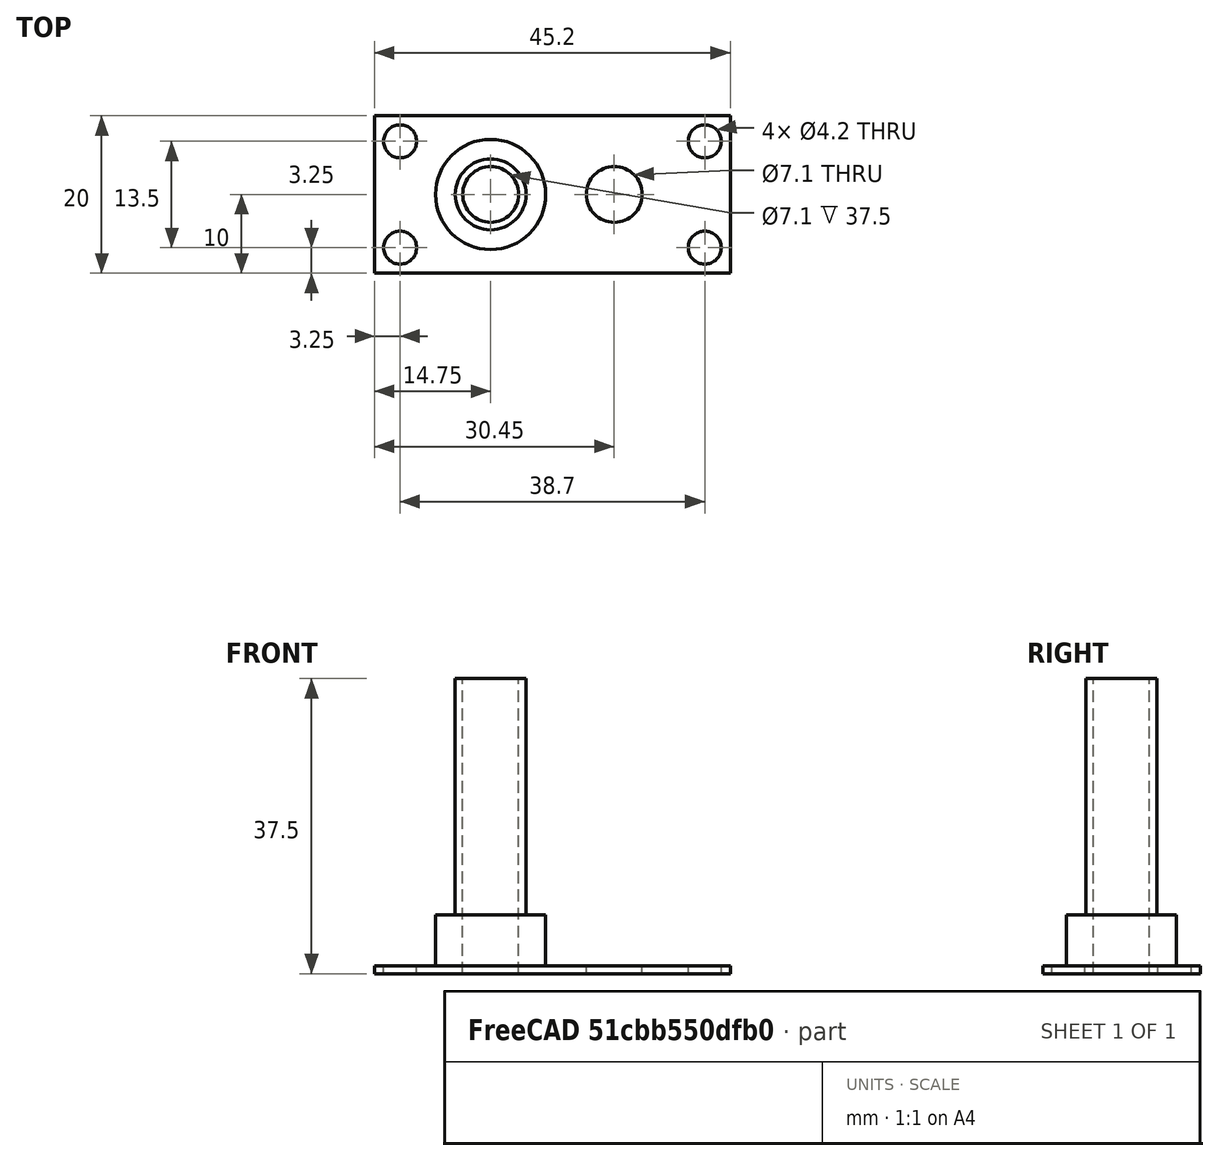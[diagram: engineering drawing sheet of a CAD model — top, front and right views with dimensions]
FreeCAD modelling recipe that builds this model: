
FCSTD DOCUMENT  (FreeCAD 0.17R13522 (Git))
Label: v5_base1_media_con_soportes
License: CreativeCommons Attribution-ShareAlike
LicenseURL: http://creativecommons.org/licenses/by-sa/4.0/
objects: Part::Cut×13, Part::Cylinder×8, Part::Box×6, Part::Feature×6, Part::Fuse×6, Part::Chamfer×3
note: 42 computed .brp shape members not serialized (recipe doc carries the construction recipe); baked Part::Feature solids carry a one-line shape summary decoded from their .brp

FEATURE [Part::Box] Box  label="base"
  AttacherType = Attacher::AttachEngine3D
  Height = 2
  Length = 45.2
  Width = 20
FEATURE [Part::Cylinder] Cylinder  label="cortador izquierda"
  Angle = 360
  AttacherType = Attacher::AttachEngine3D
  Height = 60
  Placement = pos=(14.75,10,-12) rot=(0,0,1;0rad)
  Radius = 3.55
FEATURE [Part::Feature] Cylinder001  label="cortador derecha"
  Placement = pos=(30.45,10,-4) rot=(0,0,1;0rad)
  shape: bbox 7.1 x 7.1 x 10 mm, 3 faces (baked)
FEATURE [Part::Cylinder] Cylinder002  label="sacabocado_abajo_izq"
  Angle = 360
  AttacherType = Attacher::AttachEngine3D
  Height = 10
  Placement = pos=(3,3,-4) rot=(0,0,1;0rad)
  Radius = 1.75
FEATURE [Part::Feature] Cylinder002001  label="sacabocado_abajo_derecha"
  Placement = pos=(42.2,3,-4) rot=(0,0,1;0rad)
  shape: bbox 3.5 x 3.5 x 10 mm, 3 faces (baked)
FEATURE [Part::Feature] Cylinder002002  label="sacabocado_arriba_izq"
  Placement = pos=(3,17,-4) rot=(0,0,1;0rad)
  shape: bbox 3.5 x 3.5 x 10 mm, 3 faces (baked)
FEATURE [Part::Feature] Cylinder002002001  label="sacabocado_arriba_derecha"
  Placement = pos=(42.2,17,-4) rot=(0,0,1;0rad)
  shape: bbox 3.5 x 3.5 x 10 mm, 3 faces (baked)
FEATURE [Part::Cylinder] Cylinder002002002  label="cilindro interior"
  Angle = 360
  AttacherType = Attacher::AttachEngine3D
  Height = 38.5
  Placement = pos=(14.75,10,0) rot=(0,0,1;0rad)
  Radius = 4.5
FEATURE [Part::Cylinder] Cylinder002002003  label="base cilindrica grande"
  Angle = 360
  AttacherType = Attacher::AttachEngine3D
  Height = 8.5
  Placement = pos=(14.75,10,0) rot=(0,0,1;0rad)
  Radius = 7
FEATURE [Part::Cut] Cut
  Base = -> Box
  Refine = true
  Tool = -> Cylinder002
FEATURE [Part::Cut] Cut001
  Base = -> Cut
  Refine = true
  Tool = -> Cylinder002001
FEATURE [Part::Cut] Cut002
  Base = -> Cut001
  Refine = true
  Tool = -> Cylinder001
FEATURE [Part::Cut] Cut003
  Base = -> Cut002
  Refine = true
  Tool = -> Cylinder002002001
FEATURE [Part::Cut] Cut004
  Base = -> Cut003
  Refine = true
  Tool = -> Cylinder002002
FEATURE [Part::Fuse] Fusion
  Base = -> Cylinder002002003
  Refine = true
  Tool = -> Cut004
FEATURE [Part::Fuse] Fusion001
  Base = -> Cylinder002002002
  Refine = true
  Tool = -> Fusion
FEATURE [Part::Cut] Cut005  label="pieza sin soportes"
  Base = -> Fusion001
  Refine = true
  Tool = -> Cylinder
FEATURE [Part::Box] Box001  label="soporte1"
  AttacherType = Attacher::AttachEngine3D
  Height = 10.5
  Length = 5
  Placement = pos=(36.95,7.5,-10.5) rot=(0,0,1;0rad)
  Width = 5
FEATURE [Part::Feature] Box001001  label="soporte2"
  Placement = pos=(18.95,7.5,-10.5) rot=(0,0,1;0rad)
  shape: bbox 5 x 5 x 10.5 mm, 6 faces (baked)
FEATURE [Part::Box] Box001002  label="perforador chavetas"
  AttacherType = Attacher::AttachEngine3D
  Height = 2
  Length = 30
  Placement = pos=(16,8.5,-6.3) rot=(0,0,1;0rad)
  Width = 3
FEATURE [Part::Feature] Box001002001  label="perforador chavetas001"
  Placement = pos=(16,8.5,-6.3) rot=(0,0,1;0rad)
  shape: bbox 30 x 3 x 2 mm, 6 faces (baked)
FEATURE [Part::Cut] Cut006
  Base = -> Box001
  Refine = true
  Tool = -> Box001002
FEATURE [Part::Cut] Cut007
  Base = -> Box001001
  Refine = true
  Tool = -> Box001002001
FEATURE [Part::Fuse] Fusion002
  Base = -> Cut005
  Refine = true
  Tool = -> Cut007
FEATURE [Part::Fuse] Fusion003
  Base = -> Cut006
  Refine = true
  Tool = -> Fusion002
FEATURE [Part::Chamfer] Chamfer
  Base = -> Fusion003
  Edges = 1 edges r=2: [Edge29]
FEATURE [Part::Chamfer] Chamfer001
  Base = -> Chamfer
  Edges = 1 edges r=2: [Edge19]
FEATURE [Part::Chamfer] Chamfer002  label="pieza completa"
  Base = -> Chamfer001
  Edges = 2 edges r=2: [Edge4,Edge10]
FEATURE [Part::Box] Box001002002  label="cortador separa pieza 2"
  AttacherType = Attacher::AttachEngine3D
  Height = 26
  Length = 59
  Placement = pos=(-7.65,-6,-25) rot=(0,0,1;0rad)
  Width = 30
FEATURE [Part::Cut] Cut008
  Base = -> Chamfer002
  Refine = true
  Tool = -> Box001002002
FEATURE [Part::Cylinder] Cylinder002002004  label="Cylinder"
  Angle = 360
  AttacherType = Attacher::AttachEngine3D
  Height = 10
  Placement = pos=(41.95,16.75,-4) rot=(0,0,1;0rad)
  Radius = 2.1
FEATURE [Part::Cylinder] Cylinder002002005  label="Cylinder001"
  Angle = 360
  AttacherType = Attacher::AttachEngine3D
  Height = 10
  Placement = pos=(41.95,3.25,-3) rot=(0,0,1;0rad)
  Radius = 2.1
FEATURE [Part::Cylinder] Cylinder002002006  label="Cylinder002"
  Angle = 360
  AttacherType = Attacher::AttachEngine3D
  Height = 10
  Placement = pos=(3.25,16.75,-3) rot=(0,0,1;0rad)
  Radius = 2.1
FEATURE [Part::Cylinder] Cylinder002002007  label="Cylinder003"
  Angle = 360
  AttacherType = Attacher::AttachEngine3D
  Height = 10
  Placement = pos=(3.25,3.25,-3) rot=(0,0,1;0rad)
  Radius = 2.1
FEATURE [Part::Box] Box001002003  label="Cube"
  AttacherType = Attacher::AttachEngine3D
  Height = 1
  Length = 7
  Placement = pos=(0,0,1) rot=(0,0,1;0rad)
  Width = 20
FEATURE [Part::Fuse] Fusion004
  Base = -> Cut008
  Refine = true
  Tool = -> Box001002003
FEATURE [Part::Box] Box001002004  label="Cube001"
  AttacherType = Attacher::AttachEngine3D
  Height = 1
  Length = 10
  Placement = pos=(35,0,1) rot=(0,0,1;0rad)
  Width = 20
FEATURE [Part::Fuse] Fusion005
  Base = -> Fusion004
  Refine = true
  Tool = -> Box001002004
FEATURE [Part::Cut] Cut009
  Base = -> Fusion005
  Refine = true
  Tool = -> Cylinder002002007
FEATURE [Part::Cut] Cut010
  Base = -> Cut009
  Refine = true
  Tool = -> Cylinder002002006
FEATURE [Part::Cut] Cut011
  Base = -> Cut010
  Refine = true
  Tool = -> Cylinder002002005
FEATURE [Part::Cut] Cut012
  Base = -> Cut011
  Refine = true
  Tool = -> Cylinder002002004
